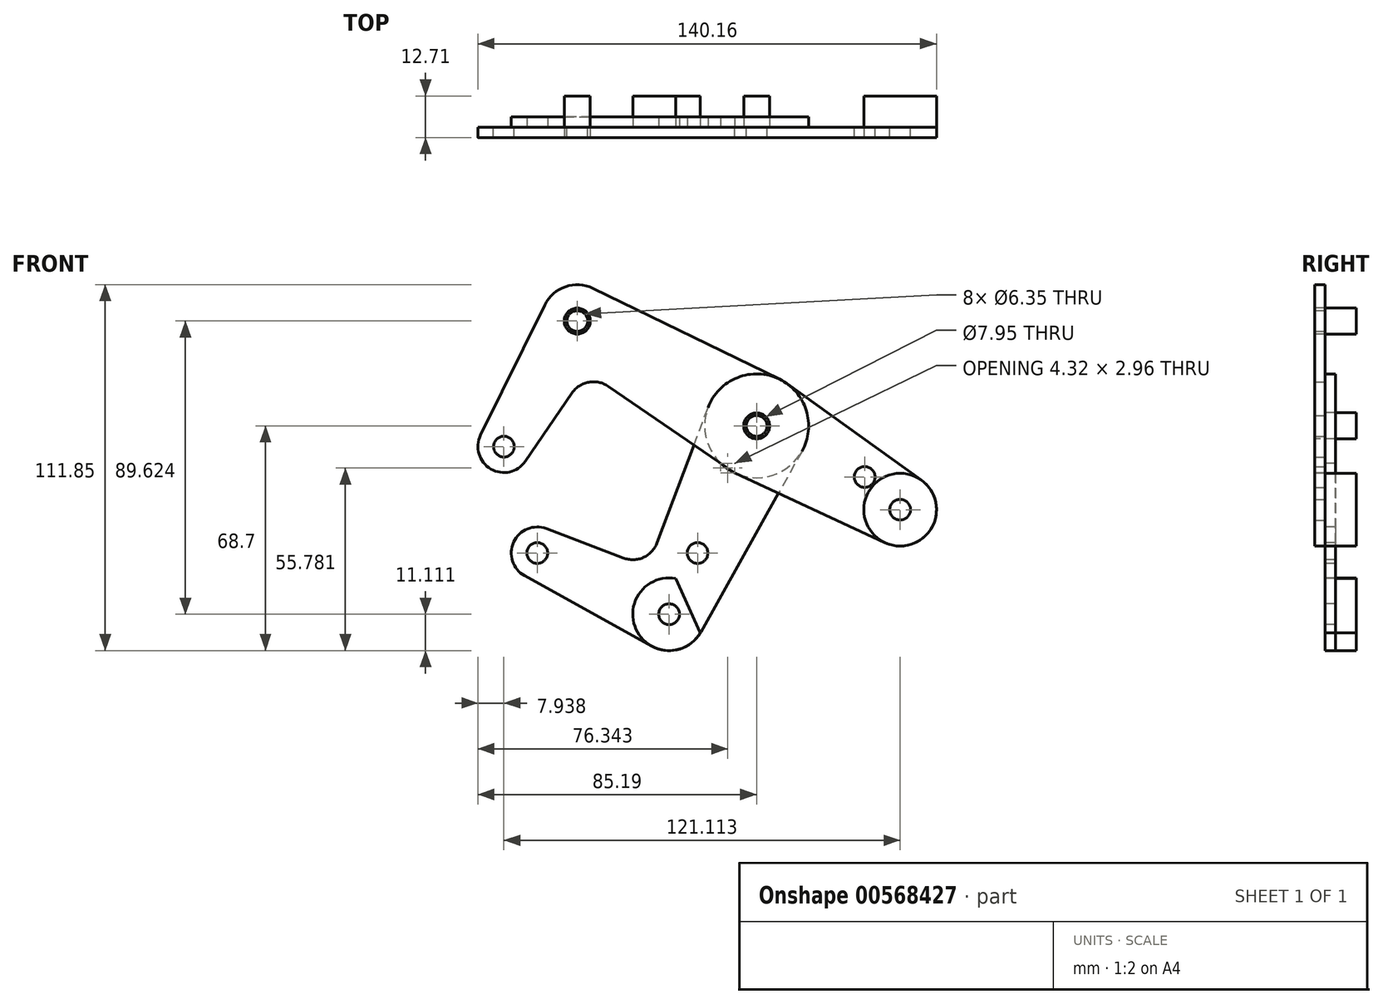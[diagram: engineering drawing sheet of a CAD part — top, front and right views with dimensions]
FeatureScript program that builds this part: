
annotation { "Feature Type Name" : "Feature", "Feature Type Description" : "" }
export const myFeature = defineFeature(function(context is Context, id is Id, definition is map)
    precondition{}
    {
        {
            var Q0;
            Q0=qCreatedBy(makeId("Front.planeOp"),FACE);
            var sketch = newSketch(context, id + "F0", { "sketchPlane" : qUnion([Q0])});
            skCircle(sketch, "E0", {"center": v(0, 0) * mm, "radius": 15.88 * mm});
            skCircle(sketch, "E1", {"center": v(0, 0) * mm, "radius": 3.98 * mm});
            skCircle(sketch, "E2", {"center": v(0, 0) * mm, "radius": 3.18 * mm});
            skLineSegment(sketch, "E3", {"start": v(-54.83, 32.04) * mm, "end": v(43.86, -25.63) * mm, "construction": true});
            skLineSegment(sketch, "E4", {"start": v(0, 0) * mm, "end": v(-26.75, -57.59) * mm, "construction": true});
            skLineSegment(sketch, "E5", {"start": v(-26.75, -57.59) * mm, "end": v(-67.07, -38.86) * mm, "construction": true});
            skLineSegment(sketch, "E6", {"start": v(-68.02, -35.83) * mm, "end": v(-77.25, -6.34) * mm, "construction": true});
            skLineSegment(sketch, "E7", {"start": v(-77.25, -6.34) * mm, "end": v(-54.83, 32.04) * mm, "construction": true});
            skCircle(sketch, "E8", {"center": v(-54.83, 32.04) * mm, "radius": 11.11 * mm});
            skCircle(sketch, "E9", {"center": v(-54.83, 32.04) * mm, "radius": 3.18 * mm});
            skCircle(sketch, "E10", {"center": v(-77.25, -6.34) * mm, "radius": 7.94 * mm});
            skCircle(sketch, "E11", {"center": v(-77.25, -6.34) * mm, "radius": 3.18 * mm});
            skCircle(sketch, "E12", {"center": v(-67.07, -38.86) * mm, "radius": 7.94 * mm});
            skCircle(sketch, "E13", {"center": v(-67.07, -38.86) * mm, "radius": 3.18 * mm});
            skCircle(sketch, "E14", {"center": v(-26.75, -57.59) * mm, "radius": 11.11 * mm});
            skCircle(sketch, "E15", {"center": v(-26.75, -57.59) * mm, "radius": 3.18 * mm});
            skCircle(sketch, "E16", {"center": v(43.86, -25.63) * mm, "radius": 3.18 * mm});
            skCircle(sketch, "E17", {"center": v(43.86, -25.63) * mm, "radius": 11.11 * mm});
            skCircle(sketch, "E18", {"center": v(-18.05, -38.86) * mm, "radius": 3.18 * mm});
            skCircle(sketch, "E19", {"center": v(33.02, -15.62) * mm, "radius": 3.18 * mm});
            skLineSegment(sketch, "E20", {"start": v(-70.7, -10.83) * mm, "end": v(-56.43, 10.03) * mm});
            skLineSegment(sketch, "E21", {"start": v(-45.37, 12.1) * mm, "end": v(-6.69, -14.4) * mm});
            skLineSegment(sketch, "E22", {"start": v(-6.69, -14.4) * mm, "end": v(39.18, -35.7) * mm});
            skLineSegment(sketch, "E23", {"start": v(6.96, 14.27) * mm, "end": v(-49.96, 42.02) * mm});
            skLineSegment(sketch, "E24", {"start": v(-64.8, 36.94) * mm, "end": v(-84.37, -2.84) * mm});
            skLineSegment(sketch, "E25", {"start": v(13.86, -7.75) * mm, "end": v(-17.06, -63.01) * mm});
            skLineSegment(sketch, "E26", {"start": v(-32.14, -67.3) * mm, "end": v(-70.92, -45.8) * mm});
            skLineSegment(sketch, "E27", {"start": v(-64.24, -31.44) * mm, "end": v(-40.69, -40.4) * mm});
            skLineSegment(sketch, "E28", {"start": v(-30.42, -35.77) * mm, "end": v(-13.9, 8.12) * mm});
            skLineSegment(sketch, "E29", {"start": v(9.26, 12.9) * mm, "end": v(50.34, -16.6) * mm});
            skArc(sketch, "E30.filletArc", {"start": v(-45.37, 12.1) * mm, "mid": v(-51.33, 13.35) * mm, "end": v(-56.43, 10.03) * mm});
            skArc(sketch, "E31.filletArc", {"start": v(-40.69, -40.4) * mm, "mid": v(-34.6, -40.22) * mm, "end": v(-30.42, -35.77) * mm});
            skSolve(sketch);
        }
        {
            var Q0;
            Q0=makeQuery(id+"F0.imprint","IMPRINT",FACE,{"disambiguationData":[TD([[makeQuery(id+"F0.imprint","IMPRINT",EDGE,{"derivedFrom":sQuery(id+"F0.wireOp",EDGE,"E9")}),-1.0]])]});
            var Q1;
            {var subQ0=sQuery(id+"F0.wireOp",EDGE,"E20");Q1=makeQuery(id+"F0.imprint","IMPRINT",FACE,{"disambiguationData":[TD([[makeQuery(id+"F0.imprint","IMPRINT",EDGE,{"derivedFrom":subQ0}),1.0]])]});}
            var Q2;
            Q2=makeQuery(id+"F0.imprint","IMPRINT",FACE,{"disambiguationData":[TD([[makeQuery(id+"F0.imprint","IMPRINT",EDGE,{"derivedFrom":sQuery(id+"F0.wireOp",EDGE,"E11")}),-1.0]])]});
            var Q3;
            {var subQ0=sQuery(id+"F0.wireOp",EDGE,"E28");var subQ1=sQuery(id+"F0.wireOp",EDGE,"E0");var subQ2=makeQuery(id+"F0.imprint","INTERSECT",VERTEX,{"derivedFrom":[subQ1,subQ0]});Q3=makeQuery(id+"F0.imprint","IMPRINT",FACE,{"disambiguationData":[TD([[makeQuery(id+"F0.imprint","IMPRINT",EDGE,{"disambiguationData":[TD([[subQ2,-1.0]])],"derivedFrom":subQ1}),-1.0]])]});}
            var Q4;
            {var subQ1=sQuery(id+"F0.wireOp",EDGE,"E0");var subQ3=sQuery(id+"F0.wireOp",EDGE,"E25");var subQ4=makeQuery(id+"F0.imprint","INTERSECT",VERTEX,{"derivedFrom":[subQ1,subQ3]});Q4=makeQuery(id+"F0.imprint","IMPRINT",FACE,{"disambiguationData":[TD([[makeQuery(id+"F0.imprint","IMPRINT",EDGE,{"disambiguationData":[TD([[subQ4,-1.0]])],"derivedFrom":subQ3}),-1.0]])]});}
            var Q5;
            Q5=makeQuery(id+"F0.imprint","IMPRINT",FACE,{"disambiguationData":[TD([[makeQuery(id+"F0.imprint","IMPRINT",EDGE,{"derivedFrom":sQuery(id+"F0.wireOp",EDGE,"E1")}),-1.0]])]});
            var Q6;
            Q6=makeQuery(id+"F0.imprint","IMPRINT",FACE,{"disambiguationData":[TD([[makeQuery(id+"F0.imprint","IMPRINT",EDGE,{"derivedFrom":sQuery(id+"F0.wireOp",EDGE,"E19")}),-1.0]])]});
            var Q7;
            Q7=makeQuery(id+"F0.imprint","IMPRINT",FACE,{"disambiguationData":[TD([[makeQuery(id+"F0.imprint","IMPRINT",EDGE,{"derivedFrom":sQuery(id+"F0.wireOp",EDGE,"E16")}),-1.0]])]});
            var Q8;
            Q8=makeQuery(id+"F0.imprint","IMPRINT",FACE,{"disambiguationData":[TD([[makeQuery(id+"F0.imprint","IMPRINT",EDGE,{"derivedFrom":sQuery(id+"F0.wireOp",EDGE,"E1")}),1.0]])]});
            extrude(context, id + "F1", {"entities" : qUnion([Q0, Q1, Q2, Q3, Q4, Q5, Q6, Q7, Q8]), "depth" : 3.17 * mm, "offsetDistance" : 25.4 * mm});
        }
        {
            var Q0;
            {var subQ1=sQuery(id+"F0.wireOp",EDGE,"E0");var subQ3=sQuery(id+"F0.wireOp",EDGE,"E25");var subQ4=makeQuery(id+"F0.imprint","INTERSECT",VERTEX,{"derivedFrom":[subQ1,subQ3]});Q0=makeQuery(id+"F0.imprint","IMPRINT",FACE,{"disambiguationData":[TD([[makeQuery(id+"F0.imprint","IMPRINT",EDGE,{"disambiguationData":[TD([[subQ4,-1.0]])],"derivedFrom":subQ3}),-1.0]])]});}
            var Q1;
            {var subQ0=sQuery(id+"F0.wireOp",EDGE,"E28");var subQ1=sQuery(id+"F0.wireOp",EDGE,"E0");var subQ2=makeQuery(id+"F0.imprint","INTERSECT",VERTEX,{"derivedFrom":[subQ1,subQ0]});Q1=makeQuery(id+"F0.imprint","IMPRINT",FACE,{"disambiguationData":[TD([[makeQuery(id+"F0.imprint","IMPRINT",EDGE,{"disambiguationData":[TD([[subQ2,-1.0]])],"derivedFrom":subQ1}),-1.0]])]});}
            var Q2;
            Q2=makeQuery(id+"F0.imprint","IMPRINT",FACE,{"disambiguationData":[TD([[makeQuery(id+"F0.imprint","IMPRINT",EDGE,{"derivedFrom":sQuery(id+"F0.wireOp",EDGE,"E1")}),-1.0]])]});
            var Q3;
            Q3=makeQuery(id+"F0.imprint","IMPRINT",FACE,{"disambiguationData":[TD([[makeQuery(id+"F0.imprint","IMPRINT",EDGE,{"derivedFrom":sQuery(id+"F0.wireOp",EDGE,"E18")}),-1.0]])]});
            var Q4;
            Q4=makeQuery(id+"F0.imprint","IMPRINT",FACE,{"disambiguationData":[TD([[makeQuery(id+"F0.imprint","IMPRINT",EDGE,{"derivedFrom":sQuery(id+"F0.wireOp",EDGE,"E15")}),-1.0]])]});
            var Q5;
            Q5=makeQuery(id+"F0.imprint","IMPRINT",FACE,{"disambiguationData":[TD([[makeQuery(id+"F0.imprint","IMPRINT",EDGE,{"derivedFrom":sQuery(id+"F0.wireOp",EDGE,"E13")}),-1.0]])]});
            extrude(context, id + "F2", {"entities" : qUnion([Q0, Q1, Q2, Q3, Q4, Q5]), "oppositeDirection" : true, "depth" : 3.17 * mm, "offsetDistance" : 25.4 * mm});
        }
        {
            var Q0;
            Q0=makeQuery(id+"F1.opExtrude","CAP_FACE",FACE,{"disambiguationData":[OSD([sQuery(id+"F0.wireOp",EDGE,"E0"),sQuery(id+"F0.wireOp",EDGE,"E1"),sQuery(id+"F0.wireOp",EDGE,"E8"),sQuery(id+"F0.wireOp",EDGE,"E9"),sQuery(id+"F0.wireOp",EDGE,"E10"),sQuery(id+"F0.wireOp",EDGE,"E11"),sQuery(id+"F0.wireOp",EDGE,"E16"),sQuery(id+"F0.wireOp",EDGE,"E17"),sQuery(id+"F0.wireOp",EDGE,"E19"),sQuery(id+"F0.wireOp",EDGE,"E20"),sQuery(id+"F0.wireOp",EDGE,"E21"),sQuery(id+"F0.wireOp",EDGE,"E22"),sQuery(id+"F0.wireOp",EDGE,"E23"),sQuery(id+"F0.wireOp",EDGE,"E24"),sQuery(id+"F0.wireOp",EDGE,"E29"),sQuery(id+"F0.wireOp",EDGE,"E30.filletArc")])],"isStart":false});
            var sketch = newSketch(context, id + "F3", { "sketchPlane" : qUnion([Q0])});
            skCircle(sketch, "E32", {"center": v(-54.83, 32.04) * mm, "radius": 3.98 * mm});
            skCircle(sketch, "E33.0", {"center": v(0, 0) * mm, "radius": 3.98 * mm});
            skCircle(sketch, "E34", {"center": v(43.86, -25.63) * mm, "radius": 11.11 * mm});
            skSolve(sketch);
        }
        {
            var Q0;
            Q0=makeQuery(id+"F0.imprint","IMPRINT",FACE,{"disambiguationData":[TD([[makeQuery(id+"F0.imprint","IMPRINT",EDGE,{"derivedFrom":sQuery(id+"F0.wireOp",EDGE,"E18")}),-1.0]])]});
            var sketch = newSketch(context, id + "F4", { "sketchPlane" : qUnion([Q0])});
            skArc(sketch, "E35.0", {"start": v(-24.73, -46.66) * mm, "mid": v(-36.88, -62.17) * mm, "end": v(-17.2, -63.28) * mm});
            skLineSegment(sketch, "E36", {"start": v(-24.73, -46.66) * mm, "end": v(-17.2, -63.28) * mm});
            skPoint(sketch, "E37.0", {"position": v(43.86, -25.63) * mm});
            skLineSegment(sketch, "E38", {"start": v(43.86, -25.63) * mm, "end": v(-20.97, -54.97) * mm, "construction": true});
            skSolve(sketch);
        }
        {
            var Q0;
            Q0=qCreatedBy(makeId("Front.planeOp"),FACE);
            cPlane(context, id + "F5", {"entities" : qUnion([Q0]), "cplaneType" : CPlaneType.OFFSET, "offset" : 9.52 * mm, "oppositeDirection" : true, "width" : 152.4 * mm, "height" : 152.4 * mm});
        }
        {
            var Q0;
            Q0=makeQuery(id+"F3.imprint","IMPRINT",FACE,{"disambiguationData":[TD([[makeQuery(id+"F3.imprint","IMPRINT",EDGE,{"derivedFrom":makeQuery(id+"F1.opExtrude","CAP_EDGE",EDGE,{"disambiguationData":[OSD([sQuery(id+"F0.wireOp",EDGE,"E9")])],"isStart":false})}),1.0]])]});
            var Q1;
            Q1=makeQuery(id+"F3.imprint","IMPRINT",FACE,{"disambiguationData":[TD([[makeQuery(id+"F3.imprint","IMPRINT",EDGE,{"derivedFrom":sQuery(id+"F3.wireOp",EDGE,"E32")}),1.0]])]});
            var Q2;
            Q2=makeQuery(id+"F3.imprint","IMPRINT",FACE,{"disambiguationData":[TD([[makeQuery(id+"F3.imprint","IMPRINT",EDGE,{"derivedFrom":makeQuery(id+"F1.opExtrude","CAP_EDGE",EDGE,{"disambiguationData":[OSD([sQuery(id+"F0.wireOp",EDGE,"E2")])],"isStart":false})}),1.0]])]});
            var Q3;
            Q3=makeQuery(id+"F3.imprint","IMPRINT",FACE,{"disambiguationData":[TD([[makeQuery(id+"F3.imprint","IMPRINT",EDGE,{"derivedFrom":sQuery(id+"F3.wireOp",EDGE,"E33.0")}),1.0]])]});
            var Q4;
            Q4=makeQuery(id+"F3.imprint","IMPRINT",FACE,{"disambiguationData":[TD([[makeQuery(id+"F3.imprint","IMPRINT",EDGE,{"derivedFrom":makeQuery(id+"F1.opExtrude","CAP_EDGE",EDGE,{"disambiguationData":[OSD([sQuery(id+"F0.wireOp",EDGE,"E16")])],"isStart":false})}),-1.0]])]});
            var Q5;
            Q5=makeQuery(id+"F3.imprint","IMPRINT",FACE,{"disambiguationData":[TD([[makeQuery(id+"F3.imprint","IMPRINT",EDGE,{"derivedFrom":makeQuery(id+"F1.opExtrude","CAP_EDGE",EDGE,{"disambiguationData":[OSD([sQuery(id+"F0.wireOp",EDGE,"E16")])],"isStart":false})}),1.0]])]});
            var Q6;
            {var subQ3=sQuery(id+"F4.wireOp",EDGE,"E36");Q6=makeQuery(id+"F4.imprint","IMPRINT",FACE,{"disambiguationData":[TD([[makeQuery(id+"F4.imprint","IMPRINT",EDGE,{"derivedFrom":subQ3}),-1.0]])]});}
            var Q7;
            Q7=qCreatedBy(id+"F5.planeOp",FACE);
            extrude(context, id + "F6", {"entities" : qUnion([Q0, Q1, Q2, Q3, Q4, Q5, Q6]), "endBound" : BoundingType.UP_TO_SURFACE, "oppositeDirection" : true, "depth" : 25.4 * mm, "endBoundEntityFace" : qUnion([Q7]), "offsetDistance" : 25.4 * mm});
        }
    });
